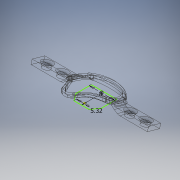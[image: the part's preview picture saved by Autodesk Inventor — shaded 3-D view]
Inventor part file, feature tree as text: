
AUTODESK INVENTOR PART (.ipt)
format: ipt  version: 2018 (Build 220112000, 112)  size: 2,534,400 bytes
history: native  units: mm
features: sketch x73, extrude x68, fillet x42, mirror x3, shell x1, hole x1
ambient origin geometry x8: Origin, YZ Plane, XZ Plane, XY Plane, X Axis, Y Axis, Z Axis, Center Point
bodies: Solid1 (feature_tree)
feature tree (188):
  extrude  "Extrusion1"  TaperAngle=0.0deg  [1 undecoded]
  extrude  "Extrusion2"  Depth=10.0mm
  extrude  "Extrusion3"  TaperAngle=0.0deg  [1 undecoded]
  shell  "Shell2"  Thickness=0.0mm
  extrude  "Extrusion4"  Depth=1.6mm
  extrude  "Extrusion6"  Depth=10.0mm TaperAngle=0.0deg
  extrude  "Extrusion7"  Depth=1.75mm
  extrude  "Extrusion8"  Depth=2.0mm
  extrude  "Extrusion9"  Depth=10.0mm TaperAngle=0.0deg
  extrude  "Extrusion11"  Depth=10.0mm TaperAngle=0.0deg
  fillet  "Fillet1"  Radius=10.0mm
  fillet  "Fillet2"  Radius=10.0mm
  fillet  "Fillet3"  [1 undecoded]
  fillet  "Fillet4"  Radius=0.541mm
  fillet  "Fillet5"  [1 undecoded]
  extrude  "Extrusion12"  Depth=7.5mm TaperAngle=0.0deg
  extrude  "Extrusion13"  TaperAngle=0.0deg  [1 undecoded]
  extrude  "Extrusion16"  Depth=51.0mm TaperAngle=0.0deg
  extrude  "Extrusion17"  TaperAngle=0.0deg  [1 undecoded]
  extrude  "Extrusion18"  Depth=10.0mm TaperAngle=0.0deg
  extrude  "Extrusion19"  Depth=10.0mm TaperAngle=0.0deg
  fillet  "Fillet6"  Radius=6.0mm
  extrude  "Extrusion20"  Depth=42.0mm TaperAngle=0.0deg
  fillet  "Fillet7"  Radius=42.0mm
  extrude  "Extrusion21"  Depth=2.6mm
  extrude  "Extrusion22"  Depth=2.6mm
  sketch  "Sketch23"  dims[d147=12.0125mm d148=12.0125mm]
  extrude  "Extrusion24"  Depth=12.0125mm
  extrude  "Extrusion26"  Depth=17.5mm
  extrude  "Extrusion28"  Depth=3.0mm
  extrude  "Extrusion32"  Depth=3.0mm
  extrude  "Extrusion37"  Depth=12.0mm TaperAngle=0.0deg
  extrude  "Extrusion38"  Depth=10.0mm TaperAngle=0.0deg
  extrude  "Extrusion40"  Depth=3.11mm
  extrude  "Extrusion41"  Depth=10.0mm TaperAngle=0.0deg
  extrude  "Extrusion42"  Depth=0.365mm TaperAngle=0.0deg
  extrude  "Extrusion43"  TaperAngle=0.0deg  [1 undecoded]
  extrude  "Extrusion44"  TaperAngle=0.0deg  [1 undecoded]
  hole  "Hole1"  [1 undecoded]
  sketch  "Sketch45"  dims[d203=20.0mm d204=15.65mm d205=0.0mm]
  extrude  "Extrusion45"  Depth=15.65mm TaperAngle=0.0deg
  extrude  "Extrusion47"  Depth=0.861mm
  mirror  "Mirror1"
  extrude  "Extrusion48"  Depth=1.61mm
  fillet  "Fillet23"  [1 undecoded]
  fillet  "Fillet24"  Radius=1.92mm
  extrude  "Extrusion49"  Depth=0.276mm
  extrude  "Extrusion50"  TaperAngle=0.0deg  [1 undecoded]
  extrude  "Extrusion54"  TaperAngle=0.0deg  [1 undecoded]
  extrude  "Extrusion55"  Depth=2.5mm
  extrude  "Extrusion56"  TaperAngle=0.0deg  [1 undecoded]
  extrude  "Extrusion57"  Depth=10.0mm TaperAngle=0.0deg
  sketch  "Sketch61"  dims[d255=2.57mm d256=2.37mm]
  extrude  "Extrusion58"  Depth=0.83mm TaperAngle=0.0deg
  extrude  "Extrusion59"  Depth=2.37mm
  extrude  "Extrusion60"  Depth=4.5mm
  fillet  "Fillet27"  Radius=0.83mm
  fillet  "Fillet28"  Radius=6.37mm
  extrude  "Extrusion61"  Depth=6.37mm TaperAngle=0.0deg
  fillet  "Fillet29"  Radius=6.71mm
  fillet  "Fillet30"  Radius=6.71mm
  fillet  "Fillet31"  [1 undecoded]
  fillet  "Fillet32"  Radius=2.0mm
  extrude  "Extrusion62"  Depth=2.0mm
  fillet  "Fillet33"  Radius=2.0mm
  fillet  "Fillet34"  Radius=2.0mm
  fillet  "Fillet35"  Radius=2.0mm
  fillet  "Fillet36"  Radius=2.0mm
  extrude  "Extrusion63"  Depth=1.9mm
  extrude  "Extrusion64"  Depth=0.616mm
  extrude  "Extrusion65"  Depth=2.0mm
  fillet  "Fillet37"  Radius=1.76mm
  fillet  "Fillet38"  [1 undecoded]
  extrude  "Extrusion69"  Depth=0.409mm
  extrude  "Extrusion70"  Depth=6.7mm TaperAngle=0.0deg
  extrude  "Extrusion71"  TaperAngle=0.0deg  [1 undecoded]
  extrude  "Extrusion72"  Depth=2.0mm
  extrude  "Extrusion73"  Depth=6.7mm TaperAngle=0.0deg
  extrude  "Extrusion74"  Depth=0.241mm
  fillet  "Fillet42"  Radius=5.47mm
  fillet  "Fillet43"  Radius=0.184mm
  extrude  "Extrusion75"  [1 undecoded]
  extrude  "Extrusion76"  [1 undecoded]
  mirror  "Mirror2"
  extrude  "Extrusion77"  [1 undecoded]
  extrude  "Extrusion78"  [1 undecoded]
  extrude  "Extrusion79"  [1 undecoded]
  mirror  "Mirror3"
  extrude  "Extrusion80"  [1 undecoded]
  extrude  "Extrusion81"  [1 undecoded]
  fillet  "Fillet44"  [1 undecoded]
  fillet  "Fillet45"  [1 undecoded]
  fillet  "Fillet46"  [1 undecoded]
  fillet  "Fillet47"  [1 undecoded]
  fillet  "Fillet48"  [1 undecoded]
  fillet  "Fillet49"  [1 undecoded]
  fillet  "Fillet50"  [1 undecoded]
  sketch  "Sketch86"
  fillet  "Fillet51"  [1 undecoded]
  fillet  "Fillet52"  [1 undecoded]
  fillet  "Fillet53"  [1 undecoded]
  fillet  "Fillet54"  [1 undecoded]
  sketch  "Sketch87"
  extrude  "Extrusion82"  [1 undecoded]
  extrude  "Extrusion83"  [1 undecoded]
  extrude  "Extrusion84"  [1 undecoded]
  fillet  "Fillet55"  [1 undecoded]
  fillet  "Fillet56"  [1 undecoded]
  extrude  "Extrusion85"  [1 undecoded]
  extrude  "Extrusion86"  [1 undecoded]
  extrude  "Extrusion87"  [1 undecoded]
  fillet  "Fillet57"  [1 undecoded]
  fillet  "Fillet58"  [1 undecoded]
  extrude  "Extrusion88"  [1 undecoded]
  extrude  "Extrusion89"  [1 undecoded]
  fillet  "Fillet59"  [1 undecoded]
  fillet  "Fillet60"  [1 undecoded]
  fillet  "Fillet61"  [1 undecoded]
  fillet  "Fillet62"  [1 undecoded]
  extrude  "Extrusion90"  [1 undecoded]
  sketch  "Sketch1"  dims[d0=10.0mm d1=0.0mm d4=0.0mm d5=0.0mm]
  sketch  "Sketch2"  dims[d6=10.0mm d7=0.0mm d9=1.2mm]
  sketch  "Sketch3"  dims[d10=0.0mm d11=0.0mm d14=0.0mm d15=0.0mm d16=0.0mm d17=0.0mm]
  sketch  "Sketch4"  dims[d18=0.0mm d19=0.0mm d20=1.6mm]
  sketch  "Sketch6"  dims[d21=0.0mm d22=0.0mm d25=10.0mm d26=0.0mm]
  sketch  "Sketch7"  dims[d27=2.23mm d28=1.75mm]
  sketch  "Sketch8"  dims[d29=2.79mm d30=2.0mm]
  sketch  "Sketch9"  dims[d31=5.19mm d32=10.0mm d33=0.0mm]
  sketch  "Sketch11"  dims[d34=10.0mm d35=0.0mm d40=10.0mm d41=0.0mm d42=10.0mm d43=0.0mm d44=10.0mm d45=0.0mm d46=0.0mm d47=0.0mm d48=0.541mm d49=0.0mm d50=0.0mm]
  sketch  "Sketch12"  dims[d51=4.84mm d52=7.5mm d53=0.0mm]
  sketch  "Sketch13"  dims[d54=0.0mm d55=0.0mm d59=0.0mm d60=0.0mm]
  sketch  "Sketch16"  dims[d78=51.0mm d79=0.0mm d84=51.0mm d85=0.0mm]
  sketch  "Sketch17"  dims[d94=51.0mm d95=0.0mm d123=0.0mm d124=0.0mm]
  sketch  "Sketch18"  dims[d125=0.0mm d126=0.0mm d131=10.0mm d132=0.0mm]
  sketch  "Sketch19"  dims[d133=10.0mm d134=0.0mm d135=10.0mm d136=0.0mm d137=6.0mm]
  sketch  "Sketch20"  dims[d138=1.9mm d139=42.0mm d140=0.0mm d141=42.0mm d142=0.0mm]
  sketch  "Sketch21"  dims[d143=2.6mm d144=2.6mm]
  sketch  "Sketch22"  dims[d145=2.6mm d146=2.6mm]
  sketch  "Sketch24"  dims[d149=17.5mm d150=17.5mm]
  sketch  "Sketch26"  dims[d151=3.0mm d152=3.0mm]
  sketch  "Sketch28"  dims[d153=3.0mm d154=3.0mm]
  sketch  "Sketch32"  dims[d155=2.6mm d156=6.0mm d157=4.4mm d158=2.0mm d159=14.3117mm d160=8.0mm d161=20.594885mm d162=12.0mm d163=0.0mm]
  sketch  "Sketch37"  dims[d170=10.0mm d171=0.0mm d172=10.0mm d173=0.0mm]
  sketch  "Sketch38"  dims[d174=3.64mm d175=3.11mm]
  sketch  "Sketch40"  dims[d176=0.0mm d177=0.0mm d178=10.0mm d179=0.0mm]
  sketch  "Sketch41"  dims[d186=0.365mm d187=0.0mm d190=0.365mm d191=0.0mm]
  sketch  "Sketch42"  dims[d192=0.0mm d193=0.0mm d194=0.0mm d195=0.0mm]
  sketch  "Sketch43"  dims[d196=0.0mm d197=0.0mm d198=0.0mm d199=0.0mm]
  sketch  "Sketch44"  dims[d200=0.0mm d201=0.0mm d202=2.0mm]
  sketch  "Sketch46"  dims[d206=0.675mm d207=0.861mm]
  sketch  "Sketch48"  dims[d208=0.8mm d209=1.61mm d210=0.0mm d211=0.0mm d212=1.92mm]
  sketch  "Sketch49"  dims[d213=2.91mm d214=0.276mm]
  sketch  "Sketch50"  dims[d215=0.425mm d218=0.0mm d219=0.0mm]
  sketch  "Sketch51"  dims[d222=10.0mm d223=0.0mm d226=0.0mm d227=0.0mm]
  sketch  "Sketch55"  dims[d228=5.04mm d229=2.5mm]
  sketch  "Sketch57"  dims[d241=10.0mm d242=0.0mm d245=0.0mm d246=0.0mm]
  sketch  "Sketch59"  dims[d247=10.0mm d248=0.0mm d249=1.22mm d250=0.0mm]
  sketch  "Sketch60"  dims[d251=0.0mm d252=0.0mm d253=0.83mm d254=0.0mm]
  sketch  "Sketch62"  dims[d257=9.0mm d258=5.320111mm d259=8.0mm d260=4.5mm d261=0.83mm d262=0.0mm d263=6.37mm d264=0.0mm]
  sketch  "Sketch63"  dims[d265=6.37mm d266=0.0mm d267=6.37mm d268=0.0mm d269=6.71mm d270=0.0mm d271=6.71mm d272=0.0mm d273=0.0mm d274=0.0mm d275=2.0mm]
  sketch  "Sketch64"  dims[d276=0.789mm d277=2.0mm d278=2.0mm d279=2.0mm d280=2.0mm d281=2.0mm]
  sketch  "Sketch65"  dims[d282=9.0mm d283=5.320111mm d284=8.0mm d285=1.9mm]
  sketch  "Sketch66"  dims[d286=0.3mm d287=0.616mm]
  sketch  "Sketch67"  dims[d288=2.0mm d289=2.0mm d290=1.76mm d291=0.0mm d292=0.0mm d293=0.0mm]
  sketch  "Sketch68"  dims[d294=0.6mm d295=0.0mm d296=0.409mm]
  sketch  "Sketch69"  dims[d297=0.323mm d298=6.7mm d299=0.0mm]
  sketch  "Sketch73"  dims[d300=6.7mm d301=0.0mm d302=0.0mm d303=0.0mm]
  sketch  "Sketch74"  dims[d304=2.0mm d305=2.0mm]
  sketch  "Sketch75"  dims[d306=0.0mm d307=0.0mm d308=6.7mm d309=0.0mm]
  sketch  "Sketch76"  dims[d310=2.0mm d311=0.241mm d312=5.47mm d313=0.184mm]
  sketch  "Sketch77"  dims[d314=0.0mm d315=0.0mm]
  sketch  "Sketch78"
  sketch  "Sketch79"
  sketch  "Sketch80"
  sketch  "Sketch81"
  sketch  "Sketch82"
  sketch  "Sketch83"
  sketch  "Sketch84"
  sketch  "Sketch85"
  sketch  "Sketch88"
  sketch  "Sketch89"
  sketch  "Sketch90"
  sketch  "Sketch91"
  sketch  "Sketch92"
  sketch  "Sketch93"
  sketch  "Sketch94"
  sketch  "Sketch95"
  sketch  "Sketch96"
note: 51 required parameter values undecoded (feature->parameter linkage not recoverable at this tier; creation-order binding heuristic only, values carry confidence <= 0.55)
